annotation { "Feature Type Name" : "Feature", "Feature Type Description" : "" }
export const myFeature = defineFeature(function(context is Context, id is Id, definition is map)
    precondition{}
    {
        {
            var Q0;
            Q0=qCreatedBy(makeId("Top.planeOp"),FACE);
            var sketch = newSketch(context, id + "F0", { "sketchPlane" : qUnion([Q0])});
            skLineSegment(sketch, "E0.bottom", {"start": v(-50.8, -50.8) * mm, "end": v(50.8, -50.8) * mm});
            skLineSegment(sketch, "E0.top", {"start": v(-50.8, 50.8) * mm, "end": v(50.8, 50.8) * mm});
            skLineSegment(sketch, "E0.left", {"start": v(-50.8, -50.8) * mm, "end": v(-50.8, 50.8) * mm});
            skLineSegment(sketch, "E0.right", {"start": v(50.8, -50.8) * mm, "end": v(50.8, 50.8) * mm});
            skPoint(sketch, "E0.middle", {"position": v(0, 0) * mm});
            skCircle(sketch, "E1.cCircle", {"center": v(0, 0) * mm, "radius": 71.84 * mm, "construction": true});
            skLineSegment(sketch, "E1.0", {"start": v(50.8, 50.8) * mm, "end": v(71.84, 0) * mm});
            skLineSegment(sketch, "E1.1", {"start": v(71.84, 0) * mm, "end": v(50.8, -50.8) * mm});
            skLineSegment(sketch, "E1.2", {"start": v(50.8, -50.8) * mm, "end": v(0, -71.84) * mm});
            skLineSegment(sketch, "E1.3", {"start": v(0, -71.84) * mm, "end": v(-50.8, -50.8) * mm});
            skLineSegment(sketch, "E1.4", {"start": v(-50.8, -50.8) * mm, "end": v(-71.84, 0) * mm});
            skLineSegment(sketch, "E1.5", {"start": v(-71.84, 0) * mm, "end": v(-50.8, 50.8) * mm});
            skLineSegment(sketch, "E1.6", {"start": v(-50.8, 50.8) * mm, "end": v(0, 71.84) * mm});
            skLineSegment(sketch, "E1.7", {"start": v(0, 71.84) * mm, "end": v(50.8, 50.8) * mm});
            skSolve(sketch);
        }
        {
            var Q0;
            Q0=makeQuery(id+"F0.imprint","IMPRINT",FACE,{"disambiguationData":[TD([[makeQuery(id+"F0.imprint","IMPRINT",EDGE,{"derivedFrom":sQuery(id+"F0.wireOp",EDGE,"E0.bottom")}),-1.0]])]});
            var Q1;
            Q1=makeQuery(id+"F0.imprint","IMPRINT",FACE,{"disambiguationData":[TD([[makeQuery(id+"F0.imprint","IMPRINT",EDGE,{"derivedFrom":sQuery(id+"F0.wireOp",EDGE,"E0.top")}),1.0]])]});
            var Q2;
            Q2=makeQuery(id+"F0.imprint","IMPRINT",FACE,{"disambiguationData":[TD([[makeQuery(id+"F0.imprint","IMPRINT",EDGE,{"derivedFrom":sQuery(id+"F0.wireOp",EDGE,"E0.left")}),1.0]])]});
            var Q3;
            Q3=makeQuery(id+"F0.imprint","IMPRINT",FACE,{"disambiguationData":[TD([[makeQuery(id+"F0.imprint","IMPRINT",EDGE,{"derivedFrom":sQuery(id+"F0.wireOp",EDGE,"E0.right")}),-1.0]])]});
            extrude(context, id + "F1", {"entities" : qUnion([Q0, Q1, Q2, Q3]), "depth" : 76.2 * mm});
        }
        {
            var Q0;
            Q0=makeQuery(id+"F0.imprint","IMPRINT",FACE,{"disambiguationData":[TD([[makeQuery(id+"F0.imprint","IMPRINT",EDGE,{"derivedFrom":sQuery(id+"F0.wireOp",EDGE,"E0.bottom")}),1.0]])]});
            extrude(context, id + "F2", {"entities" : qUnion([Q0]), "depth" : 127 * mm});
        }
        {
            var Q0;
            Q0=sQuery(id+"F0.wireOp",VERTEX,"E0.middle");
            var Q1;
            Q1=makeQuery(id+"F2.opExtrude","SWEPT_BODY",BODY,{"disambiguationData":[OSD([sQuery(id+"F0.wireOp",EDGE,"E0.bottom"),sQuery(id+"F0.wireOp",EDGE,"E0.top"),sQuery(id+"F0.wireOp",EDGE,"E0.left"),sQuery(id+"F0.wireOp",EDGE,"E0.right")])]});
            hole(context, id + "F3", {"style" : HoleStyle.SIMPLE, "endStyle" : HoleEndStyle.THROUGH, "oppositeDirection" : true, "holeDiameter" : 93.98 * mm, "tappedDepth" : 12.7 * mm, "tapClearance" : 3, "locations" : qUnion([Q0]), "scope" : qUnion([Q1])});
        }
        {
            var Q0;
            Q0=makeQuery(id+"F1.opExtrude","SWEPT_FACE",FACE,{"disambiguationData":[OSD([sQuery(id+"F0.wireOp",EDGE,"E1.2")])]});
            var sketch = newSketch(context, id + "F4", { "sketchPlane" : qUnion([Q0])});
            skPoint(sketch, "E2", {"position": v(0, 41.02) * mm});
            skSolve(sketch);
        }
        {
            var Q0;
            Q0=sQuery(id+"F4.wireOp",VERTEX,"E2");
            var Q1;
            Q1=makeQuery(id+"F2.opExtrude","SWEPT_BODY",BODY,{"disambiguationData":[OSD([sQuery(id+"F0.wireOp",EDGE,"E0.bottom"),sQuery(id+"F0.wireOp",EDGE,"E0.top"),sQuery(id+"F0.wireOp",EDGE,"E0.left"),sQuery(id+"F0.wireOp",EDGE,"E0.right")])]});
            var Q2;
            Q2=makeQuery(id+"F1.opExtrude","SWEPT_BODY",BODY,{"disambiguationData":[OSD([sQuery(id+"F0.wireOp",EDGE,"E0.bottom"),sQuery(id+"F0.wireOp",EDGE,"E1.2"),sQuery(id+"F0.wireOp",EDGE,"E1.3")])]});
            hole(context, id + "F5", {"style" : HoleStyle.SIMPLE, "endStyle" : HoleEndStyle.BLIND, "holeDiameter" : 19.05 * mm, "holeDepth" : 6.35 * mm, "tappedDepth" : 12.7 * mm, "tapClearance" : 3, "locations" : qUnion([Q0]), "scope" : qUnion([Q1, Q2])});
        }
        {
            var Q0;
            Q0=makeQuery(id+"F1.opExtrude","SWEPT_FACE",FACE,{"disambiguationData":[OSD([sQuery(id+"F0.wireOp",EDGE,"E1.3")])]});
            var sketch = newSketch(context, id + "F6", { "sketchPlane" : qUnion([Q0])});
            skLineSegment(sketch, "E3.bottom", {"start": v(-16.15, 51.57) * mm, "end": v(16.15, 51.57) * mm});
            skLineSegment(sketch, "E3.top", {"start": v(-16.15, 34.12) * mm, "end": v(16.15, 34.12) * mm});
            skLineSegment(sketch, "E3.left", {"start": v(-16.15, 51.57) * mm, "end": v(-16.15, 34.12) * mm});
            skLineSegment(sketch, "E3.right", {"start": v(16.15, 51.57) * mm, "end": v(16.15, 34.12) * mm});
            skPoint(sketch, "E3.middle", {"position": v(0, 42.84) * mm});
            skSolve(sketch);
        }
        {
            var Q0;
            Q0=makeQuery(id+"F6.imprint","IMPRINT",FACE,{"disambiguationData":[TD([[makeQuery(id+"F6.imprint","IMPRINT",EDGE,{"derivedFrom":sQuery(id+"F6.wireOp",EDGE,"E3.bottom")}),-1.0]])]});
            extrude(context, id + "F7", {"entities" : qUnion([Q0]), "operationType" : NewBodyOperationType.ADD, "depth" : 254 * mm});
        }
        {
            var Q0;
            Q0=makeQuery(id+"F1.opExtrude","SWEPT_FACE",FACE,{"disambiguationData":[OSD([sQuery(id+"F0.wireOp",EDGE,"E1.6")])]});
            var sketch = newSketch(context, id + "F8", { "sketchPlane" : qUnion([Q0])});
            skLineSegment(sketch, "E4.bottom", {"start": v(-27.5, 67.26) * mm, "end": v(27.5, 67.26) * mm});
            skLineSegment(sketch, "E4.top", {"start": v(-27.5, 9.93) * mm, "end": v(27.5, 9.93) * mm});
            skLineSegment(sketch, "E4.left", {"start": v(-27.5, 67.26) * mm, "end": v(-27.5, 9.93) * mm});
            skLineSegment(sketch, "E4.right", {"start": v(27.5, 67.26) * mm, "end": v(27.5, 9.93) * mm});
            skPoint(sketch, "E4.middle", {"position": v(0, 38.6) * mm});
            skSolve(sketch);
        }
        {
            var Q0;
            Q0=makeQuery(id+"F8.imprint","IMPRINT",FACE,{"disambiguationData":[TD([[makeQuery(id+"F8.imprint","IMPRINT",EDGE,{"derivedFrom":sQuery(id+"F8.wireOp",EDGE,"E4.bottom")}),-1.0]])]});
            extrude(context, id + "F9", {"entities" : qUnion([Q0]), "operationType" : NewBodyOperationType.ADD, "depth" : 253974.6 * mm});
        }
        {
            var Q0;
            Q0=makeQuery(id+"F1.opExtrude","SWEPT_FACE",FACE,{"disambiguationData":[OSD([sQuery(id+"F0.wireOp",EDGE,"E1.0")])]});
            var sketch = newSketch(context, id + "F10", { "sketchPlane" : qUnion([Q0])});
            skCircle(sketch, "E5", {"center": v(0, 31.98) * mm, "radius": 27.29 * mm});
            skSolve(sketch);
        }
        {
            var Q0;
            Q0=makeQuery(id+"F10.imprint","IMPRINT",FACE,{"disambiguationData":[TD([[makeQuery(id+"F10.imprint","IMPRINT",EDGE,{"derivedFrom":sQuery(id+"F10.wireOp",EDGE,"E5")}),1.0]])]});
            extrude(context, id + "F11", {"entities" : qUnion([Q0]), "operationType" : NewBodyOperationType.ADD, "depth" : 253974.6 * mm});
        }
        {
            var Q0;
            Q0=makeQuery(id+"F1.opExtrude","SWEPT_FACE",FACE,{"disambiguationData":[OSD([sQuery(id+"F0.wireOp",EDGE,"E1.7")])]});
            var sketch = newSketch(context, id + "F12", { "sketchPlane" : qUnion([Q0])});
            skCircle(sketch, "E6.cCircle", {"center": v(-3.53, 39.98) * mm, "radius": 23.82 * mm, "construction": true});
            skLineSegment(sketch, "E6.0", {"start": v(14.25, 24.13) * mm, "end": v(4.85, 17.68) * mm});
            skLineSegment(sketch, "E6.1", {"start": v(4.85, 17.68) * mm, "end": v(-6.47, 16.34) * mm});
            skLineSegment(sketch, "E6.2", {"start": v(-6.47, 16.34) * mm, "end": v(-17.12, 20.42) * mm});
            skLineSegment(sketch, "E6.3", {"start": v(-17.12, 20.42) * mm, "end": v(-24.66, 28.97) * mm});
            skLineSegment(sketch, "E6.4", {"start": v(-24.66, 28.97) * mm, "end": v(-27.35, 40.05) * mm});
            skLineSegment(sketch, "E6.5", {"start": v(-27.35, 40.05) * mm, "end": v(-24.6, 51.11) * mm});
            skLineSegment(sketch, "E6.6", {"start": v(-24.6, 51.11) * mm, "end": v(-17, 59.63) * mm});
            skLineSegment(sketch, "E6.7", {"start": v(-17, 59.63) * mm, "end": v(-6.33, 63.64) * mm});
            skLineSegment(sketch, "E6.8", {"start": v(-6.33, 63.64) * mm, "end": v(4.98, 62.23) * mm});
            skLineSegment(sketch, "E6.9", {"start": v(4.98, 62.23) * mm, "end": v(14.35, 55.72) * mm});
            skLineSegment(sketch, "E6.10", {"start": v(14.35, 55.72) * mm, "end": v(19.61, 45.61) * mm});
            skLineSegment(sketch, "E6.11", {"start": v(19.61, 45.61) * mm, "end": v(19.58, 34.21) * mm});
            skLineSegment(sketch, "E6.12", {"start": v(19.58, 34.21) * mm, "end": v(14.25, 24.13) * mm});
            skSolve(sketch);
        }
        {
            var Q0;
            Q0=makeQuery(id+"F12.imprint","IMPRINT",FACE,{"disambiguationData":[TD([[makeQuery(id+"F12.imprint","IMPRINT",EDGE,{"derivedFrom":sQuery(id+"F12.wireOp",EDGE,"E6.0")}),-1.0]])]});
            extrude(context, id + "F13", {"entities" : qUnion([Q0]), "operationType" : NewBodyOperationType.ADD, "depth" : 253974.6 * mm});
        }
        {
            var Q0;
            Q0=makeQuery(id+"F2.opExtrude","SWEPT_FACE",FACE,{"disambiguationData":[OSD([sQuery(id+"F0.wireOp",EDGE,"E0.right")])]});
            var sketch = newSketch(context, id + "F14", { "sketchPlane" : qUnion([Q0])});
            skLineSegment(sketch, "E7.bottom", {"start": v(-33.88, 87.63) * mm, "end": v(85.85, 87.63) * mm});
            skLineSegment(sketch, "E7.top", {"start": v(-33.88, 122.98) * mm, "end": v(85.85, 122.98) * mm});
            skLineSegment(sketch, "E7.left", {"start": v(-33.88, 87.63) * mm, "end": v(-33.88, 122.98) * mm});
            skLineSegment(sketch, "E7.right", {"start": v(85.85, 87.63) * mm, "end": v(85.85, 122.98) * mm});
            skPoint(sketch, "E7.middle", {"position": v(25.99, 105.3) * mm});
            skSolve(sketch);
        }
        {
            var Q0;
            {var subQ0=sQuery(id+"F14.wireOp",EDGE,"E7.left");Q0=makeQuery(id+"F14.imprint","IMPRINT",FACE,{"disambiguationData":[TD([[makeQuery(id+"F14.imprint","IMPRINT",EDGE,{"derivedFrom":subQ0}),-1.0]])]});}
            extrude(context, id + "F15", {"entities" : qUnion([Q0]), "operationType" : NewBodyOperationType.ADD, "depth" : 253974.6 * mm});
        }
        {
            var Q0;
            Q0=makeQuery(id+"F9.opExtrude","SWEPT_FACE",FACE,{"disambiguationData":[OSD([sQuery(id+"F8.wireOp",EDGE,"E4.top")])]});
            var sketch = newSketch(context, id + "F16", { "sketchPlane" : qUnion([Q0])});
            skLineSegment(sketch, "E8.bottom", {"start": v(-97238.98, -234674.56) * mm, "end": v(-97152.06, -234674.56) * mm});
            skLineSegment(sketch, "E8.top", {"start": v(-97238.98, -234616.21) * mm, "end": v(-97152.06, -234616.21) * mm});
            skLineSegment(sketch, "E8.left", {"start": v(-97238.98, -234674.56) * mm, "end": v(-97238.98, -234616.21) * mm});
            skLineSegment(sketch, "E8.right", {"start": v(-97152.06, -234674.56) * mm, "end": v(-97152.06, -234616.21) * mm});
            skPoint(sketch, "E8.middle", {"position": v(-97195.52, -234645.39) * mm});
            skSolve(sketch);
        }
        {
            var Q0;
            {var subQ5=sQuery(id+"F16.wireOp",EDGE,"E8.right");var subQ9=sQuery(id+"F16.wireOp",EDGE,"E8.top");var subQ10=makeQuery(id+"F16.imprint","INTERSECT",VERTEX,{"derivedFrom":[subQ9,subQ5]});Q0=makeQuery(id+"F16.imprint","IMPRINT",FACE,{"disambiguationData":[TD([[makeQuery(id+"F16.imprint","IMPRINT",EDGE,{"disambiguationData":[TD([[subQ10,1.0]])],"derivedFrom":subQ5}),1.0]])]});}
            extrude(context, id + "F17", {"entities" : qUnion([Q0]), "operationType" : NewBodyOperationType.ADD, "depth" : 253974.6 * mm});
        }
    });